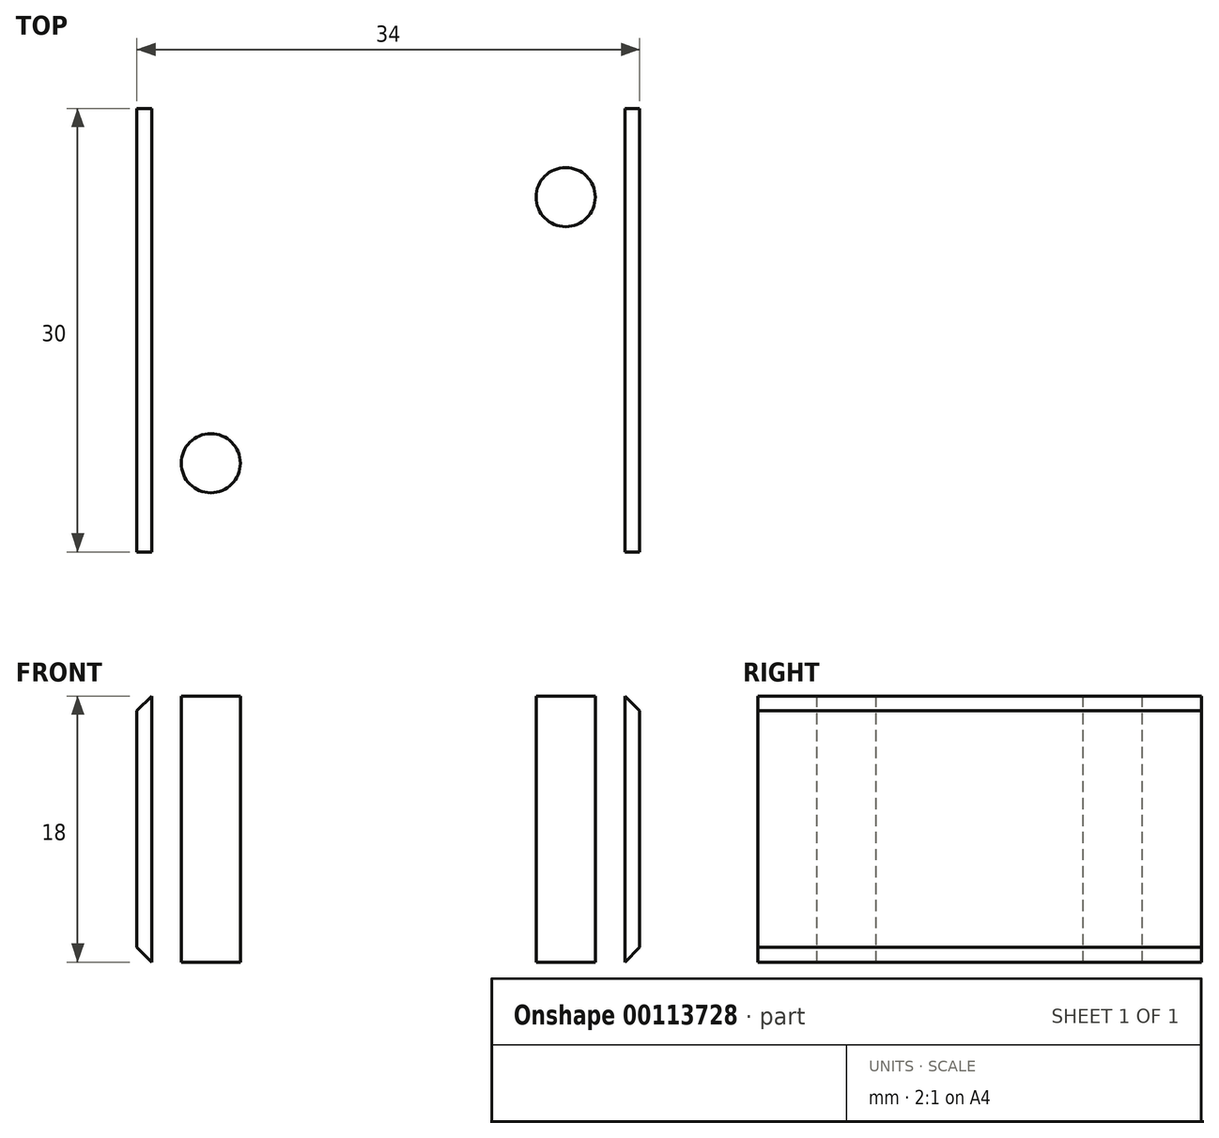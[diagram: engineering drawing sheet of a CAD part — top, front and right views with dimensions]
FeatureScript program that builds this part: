
annotation { "Feature Type Name" : "Feature", "Feature Type Description" : "" }
export const myFeature = defineFeature(function(context is Context, id is Id, definition is map)
    precondition{}
    {
        {
            var Q0;
            Q0=qCreatedBy(makeId("Front.planeOp"),FACE);
            var sketch = newSketch(context, id + "F0", { "sketchPlane" : qUnion([Q0])});
            skLineSegment(sketch, "E0.bottom", {"start": v(-46.46, 38.33) * mm, "end": v(-12.46, 38.33) * mm});
            skLineSegment(sketch, "E0.top", {"start": v(-46.46, 16.33) * mm, "end": v(-12.46, 16.33) * mm});
            skLineSegment(sketch, "E0.left", {"start": v(-46.46, 38.33) * mm, "end": v(-46.46, 16.33) * mm});
            skLineSegment(sketch, "E0.right", {"start": v(-12.46, 38.33) * mm, "end": v(-12.46, 16.33) * mm});
            skCircle(sketch, "E1", {"center": v(-29.51, 27.33) * mm, "radius": 4 * mm});
            skLineSegment(sketch, "E2", {"start": v(-29.46, 38.33) * mm, "end": v(-29.46, 16.33) * mm, "construction": true});
            skLineSegment(sketch, "E3", {"start": v(-46.46, 20.33) * mm, "end": v(-37.46, 20.33) * mm});
            skLineSegment(sketch, "E4", {"start": v(-37.46, 20.33) * mm, "end": v(-34.96, 16.33) * mm});
            skLineSegment(sketch, "E5.MirrorCS", {"start": v(-12.46, 20.33) * mm, "end": v(-21.46, 20.33) * mm});
            skLineSegment(sketch, "E6.MirrorCS", {"start": v(-21.46, 20.33) * mm, "end": v(-23.96, 16.33) * mm});
            skSolve(sketch);
        }
        {
            var Q0;
            {var subQ1=sQuery(id+"F0.wireOp",EDGE,"E0.bottom");Q0=makeQuery(id+"F0.imprint","IMPRINT",FACE,{"disambiguationData":[TD([[makeQuery(id+"F0.imprint","IMPRINT",EDGE,{"derivedFrom":subQ1}),-1.0]])]});}
            extrude(context, id + "F1", {"entities" : qUnion([Q0]), "depth" : 30 * mm});
        }
        {
            var Q0;
            Q0=makeQuery(id+"F1.opExtrude","CAP_EDGE",EDGE,{"disambiguationData":[OSD([sQuery(id+"F0.wireOp",EDGE,"E1")])],"isStart":false});
            var Q1;
            Q1=makeQuery(id+"F1.opExtrude","CAP_EDGE",EDGE,{"disambiguationData":[OSD([sQuery(id+"F0.wireOp",EDGE,"E1")])],"isStart":true});
            chamfer(context, id + "F2", {"entities" : qUnion([Q0, Q1]), "width" : 2 * mm, "tangentPropagation" : true});
        }
        {
            var Q0;
            Q0=makeQuery(id+"F1.opExtrude","SWEPT_EDGE",EDGE,{"disambiguationData":[OSD([sQuery(id+"F0.wireOp",EDGE,"E0.bottom"),sQuery(id+"F0.wireOp",EDGE,"E0.left")])]});
            var Q1;
            Q1=makeQuery(id+"F1.opExtrude","SWEPT_EDGE",EDGE,{"disambiguationData":[OSD([sQuery(id+"F0.wireOp",EDGE,"E0.bottom"),sQuery(id+"F0.wireOp",EDGE,"E0.right")])]});
            var Q2;
            Q2=makeQuery(id+"F1.opExtrude","SWEPT_EDGE",EDGE,{"disambiguationData":[OSD([sQuery(id+"F0.wireOp",EDGE,"E0.right"),sQuery(id+"F0.wireOp",EDGE,"E5.MirrorCS")])]});
            var Q3;
            Q3=makeQuery(id+"F1.opExtrude","SWEPT_EDGE",EDGE,{"disambiguationData":[OSD([sQuery(id+"F0.wireOp",EDGE,"E0.left"),sQuery(id+"F0.wireOp",EDGE,"E3")])]});
            chamfer(context, id + "F3", {"entities" : qUnion([Q0, Q1, Q2, Q3]), "width" : 1 * mm, "tangentPropagation" : true});
        }
        {
            var Q0;
            Q0=makeQuery(id+"F1.opExtrude","SWEPT_FACE",FACE,{"disambiguationData":[OSD([sQuery(id+"F0.wireOp",EDGE,"E0.bottom")])]});
            var sketch = newSketch(context, id + "F4", { "sketchPlane" : qUnion([Q0])});
            skCircle(sketch, "E7", {"center": v(-41.46, -6) * mm, "radius": 2 * mm});
            skLineSegment(sketch, "E8", {"start": v(-29.46, 0) * mm, "end": v(-29.46, -30) * mm, "construction": true});
            skLineSegment(sketch, "E9", {"start": v(-45.46, -15) * mm, "end": v(-13.46, -15) * mm, "construction": true});
            skCircle(sketch, "E10.MirrorC", {"center": v(-41.46, -24) * mm, "radius": 2 * mm});
            skCircle(sketch, "E11.MirrorC", {"center": v(-17.46, -6) * mm, "radius": 2 * mm});
            skCircle(sketch, "E12.MirrorC", {"center": v(-17.46, -24) * mm, "radius": 2 * mm});
            skSolve(sketch);
        }
        {
            var Q0;
            Q0=makeQuery(id+"F4.imprint","IMPRINT",FACE,{"disambiguationData":[TD([[makeQuery(id+"F4.imprint","IMPRINT",EDGE,{"derivedFrom":sQuery(id+"F4.wireOp",EDGE,"E7")}),1.0]])]});
            var Q1;
            Q1=makeQuery(id+"F4.imprint","IMPRINT",FACE,{"disambiguationData":[TD([[makeQuery(id+"F4.imprint","IMPRINT",EDGE,{"derivedFrom":sQuery(id+"F4.wireOp",EDGE,"E10.MirrorC")}),-1.0]])]});
            var Q2;
            Q2=makeQuery(id+"F4.imprint","IMPRINT",FACE,{"disambiguationData":[TD([[makeQuery(id+"F4.imprint","IMPRINT",EDGE,{"derivedFrom":sQuery(id+"F4.wireOp",EDGE,"E12.MirrorC")}),1.0]])]});
            var Q3;
            Q3=makeQuery(id+"F4.imprint","IMPRINT",FACE,{"disambiguationData":[TD([[makeQuery(id+"F4.imprint","IMPRINT",EDGE,{"derivedFrom":sQuery(id+"F4.wireOp",EDGE,"E11.MirrorC")}),-1.0]])]});
            extrude(context, id + "F5", {"entities" : qUnion([Q0, Q1, Q2, Q3]), "operationType" : NewBodyOperationType.REMOVE, "oppositeDirection" : true, "depth" : 25 * mm});
        }
    });
